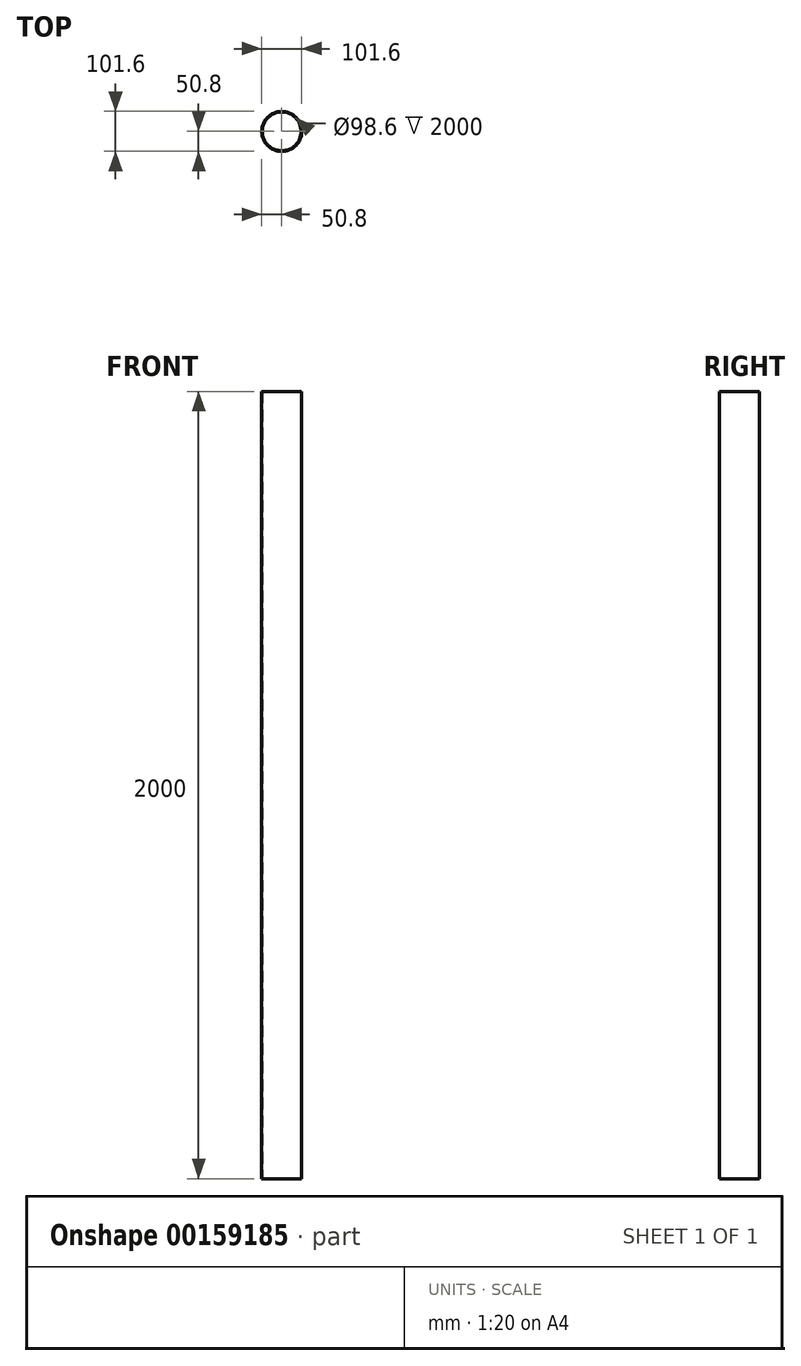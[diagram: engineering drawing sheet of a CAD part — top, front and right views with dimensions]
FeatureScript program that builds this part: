
annotation { "Feature Type Name" : "Feature", "Feature Type Description" : "" }
export const myFeature = defineFeature(function(context is Context, id is Id, definition is map)
    precondition{}
    {
        {
            var Q0;
            Q0=qCreatedBy(makeId("Top.planeOp"),FACE);
            var sketch = newSketch(context, id + "F0", { "sketchPlane" : qUnion([Q0])});
            skCircle(sketch, "E0", {"center": v(0, 0) * mm, "radius": 50.8 * mm});
            skCircle(sketch, "E1", {"center": v(0, 0) * mm, "radius": 49.3 * mm});
            skSolve(sketch);
        }
        {
            var Q0;
            Q0 = qSketchRegion(id + "F0", true);
            extrude(context, id + "F1", {"entities" : qUnion([Q0]), "depth" : 2000 * mm});
        }
    });
